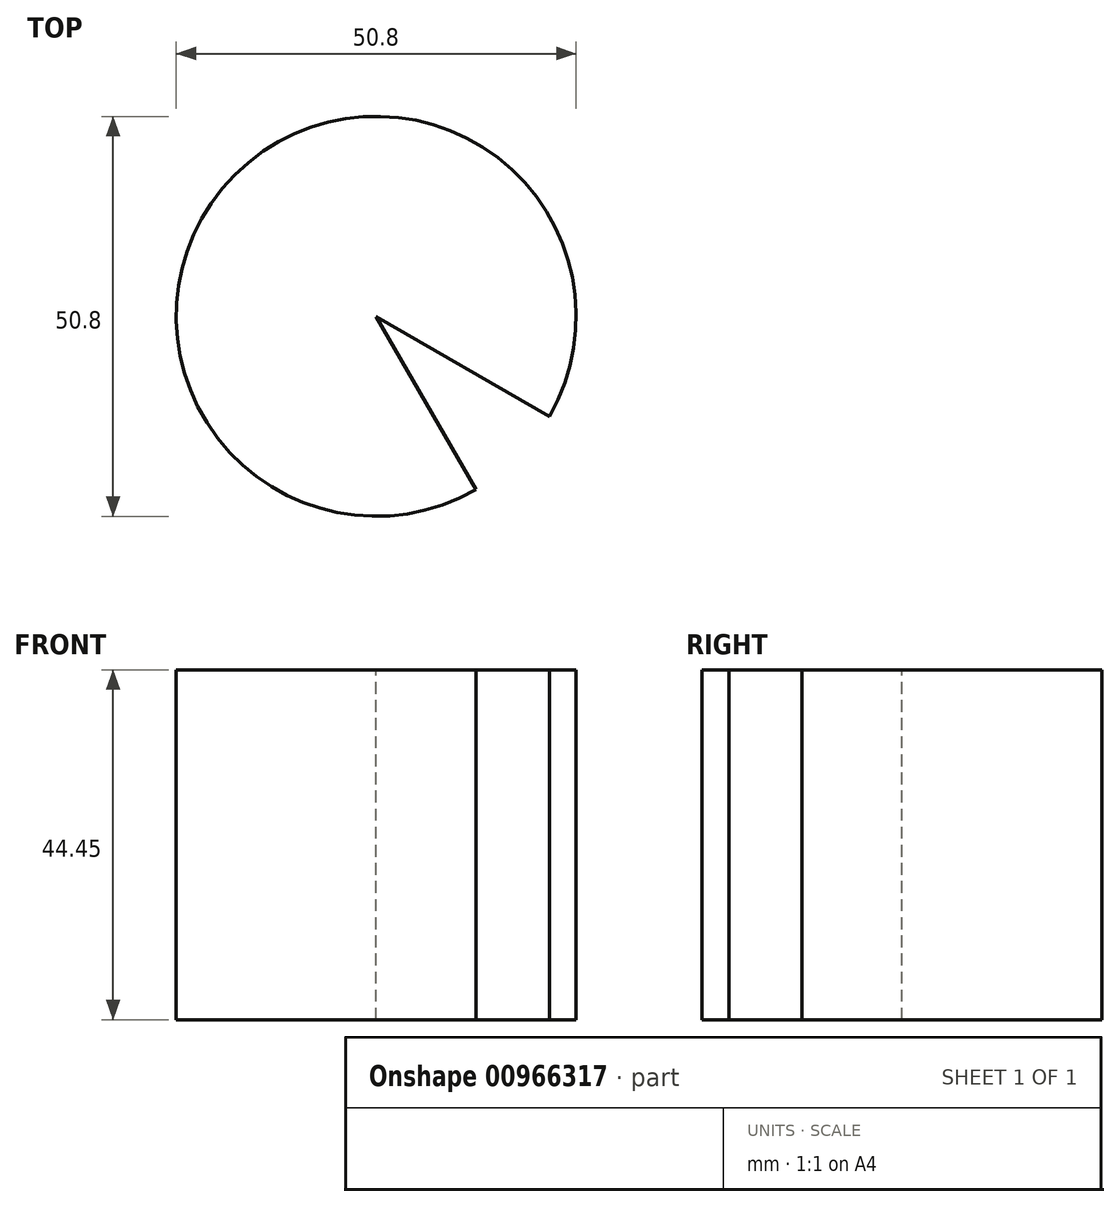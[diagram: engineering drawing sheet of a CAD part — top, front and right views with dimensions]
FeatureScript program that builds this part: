
annotation { "Feature Type Name" : "Feature", "Feature Type Description" : "" }
export const myFeature = defineFeature(function(context is Context, id is Id, definition is map)
    precondition{}
    {
        {
            var Q0;
            Q0=qCreatedBy(makeId("Front.planeOp"),FACE);
            var sketch = newSketch(context, id + "F0", { "sketchPlane" : qUnion([Q0])});
            skLineSegment(sketch, "E0", {"start": v(0, 0) * mm, "end": v(0, 44.45) * mm});
            skLineSegment(sketch, "E1", {"start": v(0, 44.45) * mm, "end": v(25.4, 44.45) * mm});
            skLineSegment(sketch, "E2", {"start": v(25.4, 44.45) * mm, "end": v(25.4, 0) * mm});
            skLineSegment(sketch, "E3", {"start": v(25.4, 0) * mm, "end": v(0, 0) * mm});
            skSolve(sketch);
        }
        {
            var Q0;
            Q0=makeQuery(id+"F0.imprint","IMPRINT",FACE,{"disambiguationData":[TD([[makeQuery(id+"F0.imprint","IMPRINT",EDGE,{"derivedFrom":sQuery(id+"F0.wireOp",EDGE,"E0")}),-1.0]])]});
            var Q1;
            Q1=sQuery(id+"F0.wireOp",EDGE,"E0");
            revolve(context, id + "F1", {"surfaceOperationType" : NewSurfaceOperationType.NEW, "entities" : qUnion([Q0]), "axis" : qUnion([Q1]), "revolveType" : RevolveType.TWO_DIRECTIONS, "angle" : 300 * degree, "angleBack" : 330 * degree});
        }
    });
